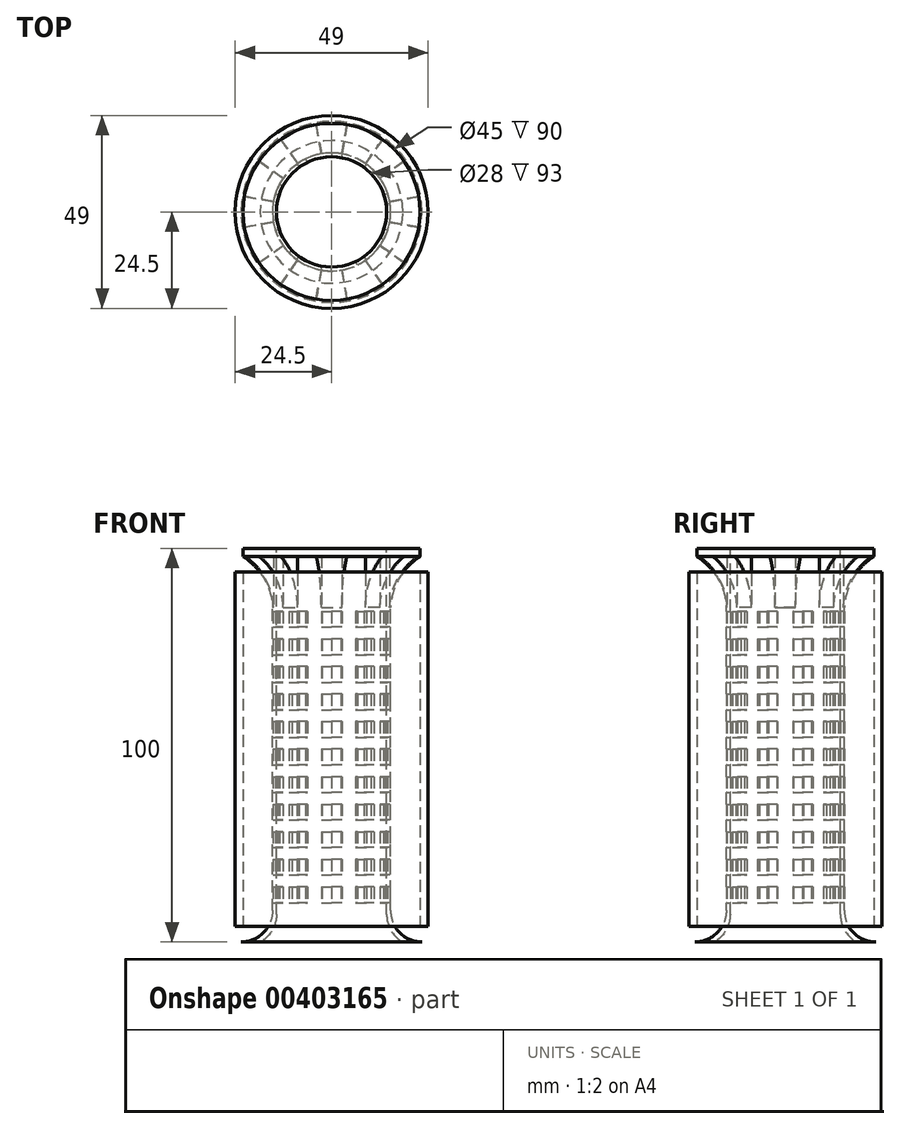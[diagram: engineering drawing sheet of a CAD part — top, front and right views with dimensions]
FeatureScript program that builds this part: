
annotation { "Feature Type Name" : "Feature", "Feature Type Description" : "" }
export const myFeature = defineFeature(function(context is Context, id is Id, definition is map)
    precondition{}
    {
        {
            var Q0;
            Q0=qCreatedBy(makeId("Top.planeOp"),FACE);
            var sketch = newSketch(context, id + "F0", { "sketchPlane" : qUnion([Q0])});
            skCircle(sketch, "E0", {"center": v(0, 0) * mm, "radius": 24.5 * mm});
            skCircle(sketch, "E1", {"center": v(0, 0) * mm, "radius": 22.5 * mm});
            skSolve(sketch);
        }
        {
            var Q0;
            Q0=qCreatedBy(makeId("Top.planeOp"),FACE);
            cPlane(context, id + "F1", {"entities" : qUnion([Q0]), "cplaneType" : CPlaneType.OFFSET, "offset" : 50 * mm, "width" : 150 * mm, "height" : 150 * mm});
        }
        {
            var Q0;
            Q0=qCreatedBy(makeId("Top.planeOp"),FACE);
            cPlane(context, id + "F2", {"entities" : qUnion([Q0]), "cplaneType" : CPlaneType.OFFSET, "offset" : 50 * mm, "oppositeDirection" : true, "width" : 150 * mm, "height" : 150 * mm});
        }
        {
            var Q0;
            Q0=qCreatedBy(makeId("Right.planeOp"),FACE);
            var sketch = newSketch(context, id + "F3", { "sketchPlane" : qUnion([Q0])});
            skLineSegment(sketch, "E2", {"start": v(0, 49) * mm, "end": v(0, -49) * mm});
            skLineSegment(sketch, "E3", {"start": v(-22.5, 49) * mm, "end": v(22.5, 49) * mm});
            skLineSegment(sketch, "E4", {"start": v(37, -49) * mm, "end": v(-37, -49) * mm});
            skLineSegment(sketch, "E5", {"start": v(14, 0) * mm, "end": v(-14, 0) * mm});
            skLineSegment(sketch, "E6.bottom", {"start": v(-14, 49) * mm, "end": v(-15, 49) * mm});
            skLineSegment(sketch, "E6.top", {"start": v(-14, -49) * mm, "end": v(-15, -49) * mm});
            skLineSegment(sketch, "E6.left", {"start": v(-14, 49) * mm, "end": v(-14, -49) * mm});
            skLineSegment(sketch, "E6.right", {"start": v(-15, 49) * mm, "end": v(-15, -49) * mm});
            skLineSegment(sketch, "E7.bottom", {"start": v(-23, -49) * mm, "end": v(-37, -49) * mm});
            skLineSegment(sketch, "E7.top", {"start": v(-22, -50) * mm, "end": v(-37, -50) * mm});
            skLineSegment(sketch, "E7.left", {"start": v(-14, -42) * mm, "end": v(-14, -45) * mm});
            skLineSegment(sketch, "E7.right", {"start": v(-37, -49) * mm, "end": v(-37, -50) * mm});
            skLineSegment(sketch, "E8.bottom", {"start": v(-37, -49) * mm, "end": v(-36, -49) * mm});
            skLineSegment(sketch, "E8.top", {"start": v(-37, -44) * mm, "end": v(-36, -44) * mm});
            skLineSegment(sketch, "E8.left", {"start": v(-37, -49) * mm, "end": v(-37, -44) * mm});
            skLineSegment(sketch, "E8.right", {"start": v(-36, -49) * mm, "end": v(-36, -44) * mm});
            skPoint(sketch, "E9.visualSharp", {"position": v(-14, -50) * mm});
            skArc(sketch, "E9.filletArc", {"start": v(-22, -50) * mm, "mid": v(-16.34, -47.66) * mm, "end": v(-14, -42) * mm});
            skLineSegment(sketch, "E10.bottom", {"start": v(-22.5, 49) * mm, "end": v(-14, 49) * mm});
            skLineSegment(sketch, "E10.top", {"start": v(-22.5, 51) * mm, "end": v(-14, 51) * mm});
            skLineSegment(sketch, "E10.left", {"start": v(-22.5, 49) * mm, "end": v(-22.5, 51) * mm});
            skLineSegment(sketch, "E10.right", {"start": v(-14, 49) * mm, "end": v(-14, 51) * mm});
            skLineSegment(sketch, "E11", {"start": v(-15, 36) * mm, "end": v(-22.5, 49) * mm});
            skLineSegment(sketch, "E12.bottom", {"start": v(-22.5, 51) * mm, "end": v(-21.5, 51) * mm});
            skLineSegment(sketch, "E12.top", {"start": v(-22.5, 59) * mm, "end": v(-21.5, 59) * mm});
            skLineSegment(sketch, "E12.left", {"start": v(-22.5, 51) * mm, "end": v(-22.5, 59) * mm});
            skLineSegment(sketch, "E12.right", {"start": v(-21.5, 51) * mm, "end": v(-21.5, 59) * mm});
            skLineSegment(sketch, "E13.bottom", {"start": v(-15, -46) * mm, "end": v(-14, -46) * mm});
            skLineSegment(sketch, "E13.top", {"start": v(-15, -49) * mm, "end": v(-14, -49) * mm});
            skLineSegment(sketch, "E13.left", {"start": v(-15, -46) * mm, "end": v(-15, -49) * mm});
            skLineSegment(sketch, "E13.right", {"start": v(-14, -46) * mm, "end": v(-14, -49) * mm});
            skLineSegment(sketch, "E14.0.1.0", {"start": v(-15, -42) * mm, "end": v(-14, -42) * mm});
            skLineSegment(sketch, "E14.0.1.1", {"start": v(-15, -39) * mm, "end": v(-14, -39) * mm});
            skLineSegment(sketch, "E14.0.2.0", {"start": v(-15, -35) * mm, "end": v(-14, -35) * mm});
            skLineSegment(sketch, "E14.0.2.1", {"start": v(-15, -32) * mm, "end": v(-14, -32) * mm});
            skLineSegment(sketch, "E14.0.3.0", {"start": v(-15, -28) * mm, "end": v(-14, -28) * mm});
            skLineSegment(sketch, "E14.0.3.1", {"start": v(-15, -25) * mm, "end": v(-14, -25) * mm});
            skLineSegment(sketch, "E14.0.4.0", {"start": v(-15, -21) * mm, "end": v(-14, -21) * mm});
            skLineSegment(sketch, "E14.0.4.1", {"start": v(-15, -18) * mm, "end": v(-14, -18) * mm});
            skLineSegment(sketch, "E14.0.5.0", {"start": v(-15, -14) * mm, "end": v(-14, -14) * mm});
            skLineSegment(sketch, "E14.0.5.1", {"start": v(-15, -11) * mm, "end": v(-14, -11) * mm});
            skLineSegment(sketch, "E14.0.6.0", {"start": v(-15, -7) * mm, "end": v(-14, -7) * mm});
            skLineSegment(sketch, "E14.0.6.1", {"start": v(-15, -4) * mm, "end": v(-14, -4) * mm});
            skLineSegment(sketch, "E14.0.7.0", {"start": v(-15, 0) * mm, "end": v(-14, 0) * mm});
            skLineSegment(sketch, "E14.0.7.1", {"start": v(-15, 3) * mm, "end": v(-14, 3) * mm});
            skLineSegment(sketch, "E14.0.8.0", {"start": v(-15, 7) * mm, "end": v(-14, 7) * mm});
            skLineSegment(sketch, "E14.0.8.1", {"start": v(-15, 10) * mm, "end": v(-14, 10) * mm});
            skLineSegment(sketch, "E14.0.9.0", {"start": v(-15, 14) * mm, "end": v(-14, 14) * mm});
            skLineSegment(sketch, "E14.0.9.1", {"start": v(-15, 17) * mm, "end": v(-14, 17) * mm});
            skLineSegment(sketch, "E14.0.10.0", {"start": v(-15, 21) * mm, "end": v(-14, 21) * mm});
            skLineSegment(sketch, "E14.0.10.1", {"start": v(-15, 24) * mm, "end": v(-14, 24) * mm});
            skLineSegment(sketch, "E14.0.11.0", {"start": v(-15, 28) * mm, "end": v(-14, 28) * mm});
            skLineSegment(sketch, "E14.0.11.1", {"start": v(-15, 31) * mm, "end": v(-14, 31) * mm});
            skLineSegment(sketch, "E14.0.12.0", {"start": v(-15, 35) * mm, "end": v(-14, 35) * mm});
            skLineSegment(sketch, "E14.0.12.1", {"start": v(-15, 38) * mm, "end": v(-14, 38) * mm});
            skLineSegment(sketch, "E14.direction1", {"start": v(-16, -49) * mm, "end": v(9, -49) * mm, "construction": true});
            skLineSegment(sketch, "E14.direction2", {"start": v(-15, -42) * mm, "end": v(-15, -41) * mm, "construction": true});
            skPoint(sketch, "E15.newPointB", {"position": v(-15, -49) * mm});
            skArc(sketch, "E15.filletArc", {"start": v(-23, -49) * mm, "mid": v(-17.34, -46.66) * mm, "end": v(-15, -41) * mm});
            skArc(sketch, "E16", {"start": v(-15, 36) * mm, "mid": v(-17.17, 43.42) * mm, "end": v(-22.5, 49) * mm});
            skSolve(sketch);
        }
        {
            var Q0;
            Q0=makeQuery(id+"F3.imprint","IMPRINT",FACE,{"disambiguationData":[TD([[makeQuery(id+"F3.imprint","IMPRINT",EDGE,{"derivedFrom":sQuery(id+"F3.wireOp",EDGE,"E12.bottom")}),1.0]])]});
            var Q1;
            {var subQ0=sQuery(id+"F3.wireOp",EDGE,"E14.0.8.1");Q1=makeQuery(id+"F3.imprint","IMPRINT",FACE,{"disambiguationData":[TD([[makeQuery(id+"F3.imprint","IMPRINT",EDGE,{"derivedFrom":subQ0}),1.0]])]});}
            var Q2;
            {var subQ0=sQuery(id+"F3.wireOp",EDGE,"E14.0.7.1");Q2=makeQuery(id+"F3.imprint","IMPRINT",FACE,{"disambiguationData":[TD([[makeQuery(id+"F3.imprint","IMPRINT",EDGE,{"derivedFrom":subQ0}),1.0]])]});}
            var Q3;
            {var subQ0=sQuery(id+"F3.wireOp",EDGE,"E14.0.11.1");Q3=makeQuery(id+"F3.imprint","IMPRINT",FACE,{"disambiguationData":[TD([[makeQuery(id+"F3.imprint","IMPRINT",EDGE,{"derivedFrom":subQ0}),1.0]])]});}
            var Q4;
            {var subQ3=sQuery(id+"F3.wireOp",EDGE,"E14.0.12.1");Q4=makeQuery(id+"F3.imprint","IMPRINT",FACE,{"disambiguationData":[TD([[makeQuery(id+"F3.imprint","IMPRINT",EDGE,{"derivedFrom":subQ3}),1.0]])]});}
            var Q5;
            {var subQ0=sQuery(id+"F3.wireOp",EDGE,"E14.0.4.1");Q5=makeQuery(id+"F3.imprint","IMPRINT",FACE,{"disambiguationData":[TD([[makeQuery(id+"F3.imprint","IMPRINT",EDGE,{"derivedFrom":subQ0}),1.0]])]});}
            var Q6;
            {var subQ0=sQuery(id+"F3.wireOp",EDGE,"E14.0.9.1");Q6=makeQuery(id+"F3.imprint","IMPRINT",FACE,{"disambiguationData":[TD([[makeQuery(id+"F3.imprint","IMPRINT",EDGE,{"derivedFrom":subQ0}),1.0]])]});}
            var Q7;
            {var subQ0=sQuery(id+"F3.wireOp",EDGE,"E14.0.3.1");Q7=makeQuery(id+"F3.imprint","IMPRINT",FACE,{"disambiguationData":[TD([[makeQuery(id+"F3.imprint","IMPRINT",EDGE,{"derivedFrom":subQ0}),1.0]])]});}
            var Q8;
            {var subQ0=sQuery(id+"F3.wireOp",EDGE,"E14.0.10.1");Q8=makeQuery(id+"F3.imprint","IMPRINT",FACE,{"disambiguationData":[TD([[makeQuery(id+"F3.imprint","IMPRINT",EDGE,{"derivedFrom":subQ0}),1.0]])]});}
            var Q9;
            Q9=makeQuery(id+"F3.imprint","IMPRINT",FACE,{"disambiguationData":[TD([[makeQuery(id+"F3.imprint","IMPRINT",EDGE,{"derivedFrom":sQuery(id+"F3.wireOp",EDGE,"E10.top")}),-1.0]])]});
            var Q10;
            {var subQ0=sQuery(id+"F3.wireOp",EDGE,"E14.0.2.1");Q10=makeQuery(id+"F3.imprint","IMPRINT",FACE,{"disambiguationData":[TD([[makeQuery(id+"F3.imprint","IMPRINT",EDGE,{"derivedFrom":subQ0}),1.0]])]});}
            var Q11;
            {var subQ0=sQuery(id+"F3.wireOp",EDGE,"E14.0.1.1");Q11=makeQuery(id+"F3.imprint","IMPRINT",FACE,{"disambiguationData":[TD([[makeQuery(id+"F3.imprint","IMPRINT",EDGE,{"derivedFrom":subQ0}),1.0]])]});}
            var Q12;
            {var subQ0=sQuery(id+"F3.wireOp",EDGE,"E14.0.6.0");Q12=makeQuery(id+"F3.imprint","IMPRINT",FACE,{"disambiguationData":[TD([[makeQuery(id+"F3.imprint","IMPRINT",EDGE,{"derivedFrom":subQ0}),1.0]])]});}
            var Q13;
            {var subQ0=sQuery(id+"F3.wireOp",EDGE,"E14.0.8.0");Q13=makeQuery(id+"F3.imprint","IMPRINT",FACE,{"disambiguationData":[TD([[makeQuery(id+"F3.imprint","IMPRINT",EDGE,{"derivedFrom":subQ0}),1.0]])]});}
            var Q14;
            {var subQ0=sQuery(id+"F3.wireOp",EDGE,"E14.0.3.0");Q14=makeQuery(id+"F3.imprint","IMPRINT",FACE,{"disambiguationData":[TD([[makeQuery(id+"F3.imprint","IMPRINT",EDGE,{"derivedFrom":subQ0}),1.0]])]});}
            var Q15;
            {var subQ2=sQuery(id+"F3.wireOp",EDGE,"E14.0.6.1");Q15=makeQuery(id+"F3.imprint","IMPRINT",FACE,{"disambiguationData":[TD([[makeQuery(id+"F3.imprint","IMPRINT",EDGE,{"derivedFrom":subQ2}),1.0]])]});}
            var Q16;
            {var subQ0=sQuery(id+"F3.wireOp",EDGE,"E14.0.9.0");Q16=makeQuery(id+"F3.imprint","IMPRINT",FACE,{"disambiguationData":[TD([[makeQuery(id+"F3.imprint","IMPRINT",EDGE,{"derivedFrom":subQ0}),1.0]])]});}
            var Q17;
            {var subQ0=sQuery(id+"F3.wireOp",EDGE,"E14.0.5.1");Q17=makeQuery(id+"F3.imprint","IMPRINT",FACE,{"disambiguationData":[TD([[makeQuery(id+"F3.imprint","IMPRINT",EDGE,{"derivedFrom":subQ0}),1.0]])]});}
            var Q18;
            {var subQ0=sQuery(id+"F3.wireOp",EDGE,"E14.0.1.0");Q18=makeQuery(id+"F3.imprint","IMPRINT",FACE,{"disambiguationData":[TD([[makeQuery(id+"F3.imprint","IMPRINT",EDGE,{"derivedFrom":subQ0}),1.0]])]});}
            var Q19;
            {var subQ0=sQuery(id+"F3.wireOp",EDGE,"E14.0.10.0");Q19=makeQuery(id+"F3.imprint","IMPRINT",FACE,{"disambiguationData":[TD([[makeQuery(id+"F3.imprint","IMPRINT",EDGE,{"derivedFrom":subQ0}),1.0]])]});}
            var Q20;
            {var subQ0=sQuery(id+"F3.wireOp",EDGE,"E14.0.11.0");Q20=makeQuery(id+"F3.imprint","IMPRINT",FACE,{"disambiguationData":[TD([[makeQuery(id+"F3.imprint","IMPRINT",EDGE,{"derivedFrom":subQ0}),1.0]])]});}
            var Q21;
            {var subQ0=sQuery(id+"F3.wireOp",EDGE,"E14.0.7.0");Q21=makeQuery(id+"F3.imprint","IMPRINT",FACE,{"disambiguationData":[TD([[makeQuery(id+"F3.imprint","IMPRINT",EDGE,{"derivedFrom":subQ0}),1.0]])]});}
            var Q22;
            {var subQ0=sQuery(id+"F3.wireOp",EDGE,"E14.0.4.0");Q22=makeQuery(id+"F3.imprint","IMPRINT",FACE,{"disambiguationData":[TD([[makeQuery(id+"F3.imprint","IMPRINT",EDGE,{"derivedFrom":subQ0}),1.0]])]});}
            var Q23;
            {var subQ2=sQuery(id+"F3.wireOp",EDGE,"E14.0.12.0");Q23=makeQuery(id+"F3.imprint","IMPRINT",FACE,{"disambiguationData":[TD([[makeQuery(id+"F3.imprint","IMPRINT",EDGE,{"derivedFrom":subQ2}),1.0]])]});}
            var Q24;
            {var subQ0=sQuery(id+"F3.wireOp",EDGE,"E14.0.2.0");Q24=makeQuery(id+"F3.imprint","IMPRINT",FACE,{"disambiguationData":[TD([[makeQuery(id+"F3.imprint","IMPRINT",EDGE,{"derivedFrom":subQ0}),1.0]])]});}
            var Q25;
            {var subQ0=sQuery(id+"F3.wireOp",EDGE,"E14.0.5.0");Q25=makeQuery(id+"F3.imprint","IMPRINT",FACE,{"disambiguationData":[TD([[makeQuery(id+"F3.imprint","IMPRINT",EDGE,{"derivedFrom":subQ0}),1.0]])]});}
            var Q26;
            Q26=makeQuery(id+"F3.imprint","IMPRINT",FACE,{"disambiguationData":[TD([[makeQuery(id+"F3.imprint","IMPRINT",EDGE,{"derivedFrom":sQuery(id+"F3.wireOp",EDGE,"E7.bottom")}),1.0]])]});
            var Q27;
            Q27=makeQuery(id+"F3.imprint","IMPRINT",FACE,{"disambiguationData":[TD([[makeQuery(id+"F3.imprint","IMPRINT",EDGE,{"derivedFrom":sQuery(id+"F3.wireOp",EDGE,"E8.bottom")}),1.0]])]});
            var Q28;
            {var subQ6=sQuery(id+"F3.wireOp",EDGE,"E15.filletArc");Q28=makeQuery(id+"F3.imprint","IMPRINT",FACE,{"disambiguationData":[TD([[makeQuery(id+"F3.imprint","IMPRINT",EDGE,{"derivedFrom":subQ6}),-1.0]])]});}
            var Q29;
            {var subQ0=sQuery(id+"F3.wireOp",EDGE,"E14.0.1.0");Q29=makeQuery(id+"F3.imprint","IMPRINT",FACE,{"disambiguationData":[TD([[makeQuery(id+"F3.imprint","IMPRINT",EDGE,{"derivedFrom":subQ0}),-1.0]])]});}
            var Q30;
            Q30=sQuery(id+"F3.wireOp",EDGE,"E2");
            revolve(context, id + "F4", {"entities" : qUnion([Q0, Q1, Q2, Q3, Q4, Q5, Q6, Q7, Q8, Q9, Q10, Q11, Q12, Q13, Q14, Q15, Q16, Q17, Q18, Q19, Q20, Q21, Q22, Q23, Q24, Q25, Q26, Q27, Q28, Q29]), "axis" : qUnion([Q30]), "revolveType" : RevolveType.FULL});
        }
        {
            var Q0;
            {var subQ0=sQuery(id+"F3.wireOp",EDGE,"E13.bottom");Q0=makeQuery(id+"F3.imprint","IMPRINT",FACE,{"disambiguationData":[TD([[makeQuery(id+"F3.imprint","IMPRINT",EDGE,{"derivedFrom":subQ0}),1.0]])]});}
            var Q1;
            {var subQ0=sQuery(id+"F3.wireOp",EDGE,"E14.0.1.1");Q1=makeQuery(id+"F3.imprint","IMPRINT",FACE,{"disambiguationData":[TD([[makeQuery(id+"F3.imprint","IMPRINT",EDGE,{"derivedFrom":subQ0}),1.0]])]});}
            var Q2;
            {var subQ0=sQuery(id+"F3.wireOp",EDGE,"E14.0.2.1");Q2=makeQuery(id+"F3.imprint","IMPRINT",FACE,{"disambiguationData":[TD([[makeQuery(id+"F3.imprint","IMPRINT",EDGE,{"derivedFrom":subQ0}),1.0]])]});}
            var Q3;
            {var subQ0=sQuery(id+"F3.wireOp",EDGE,"E14.0.3.1");Q3=makeQuery(id+"F3.imprint","IMPRINT",FACE,{"disambiguationData":[TD([[makeQuery(id+"F3.imprint","IMPRINT",EDGE,{"derivedFrom":subQ0}),1.0]])]});}
            var Q4;
            {var subQ0=sQuery(id+"F3.wireOp",EDGE,"E14.0.4.1");Q4=makeQuery(id+"F3.imprint","IMPRINT",FACE,{"disambiguationData":[TD([[makeQuery(id+"F3.imprint","IMPRINT",EDGE,{"derivedFrom":subQ0}),1.0]])]});}
            var Q5;
            {var subQ0=sQuery(id+"F3.wireOp",EDGE,"E14.0.5.1");Q5=makeQuery(id+"F3.imprint","IMPRINT",FACE,{"disambiguationData":[TD([[makeQuery(id+"F3.imprint","IMPRINT",EDGE,{"derivedFrom":subQ0}),1.0]])]});}
            var Q6;
            {var subQ2=sQuery(id+"F3.wireOp",EDGE,"E14.0.6.1");Q6=makeQuery(id+"F3.imprint","IMPRINT",FACE,{"disambiguationData":[TD([[makeQuery(id+"F3.imprint","IMPRINT",EDGE,{"derivedFrom":subQ2}),1.0]])]});}
            var Q7;
            {var subQ0=sQuery(id+"F3.wireOp",EDGE,"E14.0.7.1");Q7=makeQuery(id+"F3.imprint","IMPRINT",FACE,{"disambiguationData":[TD([[makeQuery(id+"F3.imprint","IMPRINT",EDGE,{"derivedFrom":subQ0}),1.0]])]});}
            var Q8;
            {var subQ0=sQuery(id+"F3.wireOp",EDGE,"E14.0.8.1");Q8=makeQuery(id+"F3.imprint","IMPRINT",FACE,{"disambiguationData":[TD([[makeQuery(id+"F3.imprint","IMPRINT",EDGE,{"derivedFrom":subQ0}),1.0]])]});}
            var Q9;
            {var subQ0=sQuery(id+"F3.wireOp",EDGE,"E14.0.9.1");Q9=makeQuery(id+"F3.imprint","IMPRINT",FACE,{"disambiguationData":[TD([[makeQuery(id+"F3.imprint","IMPRINT",EDGE,{"derivedFrom":subQ0}),1.0]])]});}
            var Q10;
            {var subQ0=sQuery(id+"F3.wireOp",EDGE,"E14.0.10.1");Q10=makeQuery(id+"F3.imprint","IMPRINT",FACE,{"disambiguationData":[TD([[makeQuery(id+"F3.imprint","IMPRINT",EDGE,{"derivedFrom":subQ0}),1.0]])]});}
            var Q11;
            {var subQ0=sQuery(id+"F3.wireOp",EDGE,"E14.0.11.1");Q11=makeQuery(id+"F3.imprint","IMPRINT",FACE,{"disambiguationData":[TD([[makeQuery(id+"F3.imprint","IMPRINT",EDGE,{"derivedFrom":subQ0}),1.0]])]});}
            var Q12;
            Q12=sQuery(id+"F3.wireOp",EDGE,"E2");
            revolve(context, id + "F5", {"entities" : qUnion([Q0, Q1, Q2, Q3, Q4, Q5, Q6, Q7, Q8, Q9, Q10, Q11]), "axis" : qUnion([Q12]), "revolveType" : RevolveType.ONE_DIRECTION, "angle" : 10 * degree});
        }
        {
            var Q0;
            Q0=makeQuery(id+"F5.opRevolve","SWEPT_BODY",BODY,{"disambiguationData":[OSD([sQuery(id+"F3.wireOp",EDGE,"E6.left"),sQuery(id+"F3.wireOp",EDGE,"E6.right"),sQuery(id+"F3.wireOp",EDGE,"E14.0.11.1"),sQuery(id+"F3.wireOp",EDGE,"E14.0.12.0")])]});
            var Q1;
            Q1=makeQuery(id+"F5.opRevolve","SWEPT_BODY",BODY,{"disambiguationData":[OSD([sQuery(id+"F3.wireOp",EDGE,"E6.left"),sQuery(id+"F3.wireOp",EDGE,"E6.right"),sQuery(id+"F3.wireOp",EDGE,"E14.0.10.1"),sQuery(id+"F3.wireOp",EDGE,"E14.0.11.0")])]});
            var Q2;
            Q2=makeQuery(id+"F5.opRevolve","SWEPT_BODY",BODY,{"disambiguationData":[OSD([sQuery(id+"F3.wireOp",EDGE,"E6.left"),sQuery(id+"F3.wireOp",EDGE,"E6.right"),sQuery(id+"F3.wireOp",EDGE,"E14.0.9.1"),sQuery(id+"F3.wireOp",EDGE,"E14.0.10.0")])]});
            var Q3;
            Q3=makeQuery(id+"F5.opRevolve","SWEPT_BODY",BODY,{"disambiguationData":[OSD([sQuery(id+"F3.wireOp",EDGE,"E6.left"),sQuery(id+"F3.wireOp",EDGE,"E6.right"),sQuery(id+"F3.wireOp",EDGE,"E14.0.8.1"),sQuery(id+"F3.wireOp",EDGE,"E14.0.9.0")])]});
            var Q4;
            Q4=makeQuery(id+"F5.opRevolve","SWEPT_BODY",BODY,{"disambiguationData":[OSD([sQuery(id+"F3.wireOp",EDGE,"E6.left"),sQuery(id+"F3.wireOp",EDGE,"E6.right"),sQuery(id+"F3.wireOp",EDGE,"E14.0.7.1"),sQuery(id+"F3.wireOp",EDGE,"E14.0.8.0")])]});
            var Q5;
            Q5=makeQuery(id+"F5.opRevolve","SWEPT_BODY",BODY,{"disambiguationData":[OSD([sQuery(id+"F3.wireOp",EDGE,"E6.left"),sQuery(id+"F3.wireOp",EDGE,"E6.right"),sQuery(id+"F3.wireOp",EDGE,"E14.0.6.1"),sQuery(id+"F3.wireOp",EDGE,"E14.0.7.0")])]});
            var Q6;
            Q6=makeQuery(id+"F5.opRevolve","SWEPT_BODY",BODY,{"disambiguationData":[OSD([sQuery(id+"F3.wireOp",EDGE,"E6.left"),sQuery(id+"F3.wireOp",EDGE,"E6.right"),sQuery(id+"F3.wireOp",EDGE,"E14.0.5.1"),sQuery(id+"F3.wireOp",EDGE,"E14.0.6.0")])]});
            var Q7;
            Q7=makeQuery(id+"F5.opRevolve","SWEPT_BODY",BODY,{"disambiguationData":[OSD([sQuery(id+"F3.wireOp",EDGE,"E6.left"),sQuery(id+"F3.wireOp",EDGE,"E6.right"),sQuery(id+"F3.wireOp",EDGE,"E14.0.4.1"),sQuery(id+"F3.wireOp",EDGE,"E14.0.5.0")])]});
            var Q8;
            Q8=makeQuery(id+"F5.opRevolve","SWEPT_BODY",BODY,{"disambiguationData":[OSD([sQuery(id+"F3.wireOp",EDGE,"E6.left"),sQuery(id+"F3.wireOp",EDGE,"E6.right"),sQuery(id+"F3.wireOp",EDGE,"E14.0.3.1"),sQuery(id+"F3.wireOp",EDGE,"E14.0.4.0")])]});
            var Q9;
            Q9=makeQuery(id+"F5.opRevolve","SWEPT_BODY",BODY,{"disambiguationData":[OSD([sQuery(id+"F3.wireOp",EDGE,"E6.left"),sQuery(id+"F3.wireOp",EDGE,"E6.right"),sQuery(id+"F3.wireOp",EDGE,"E14.0.2.1"),sQuery(id+"F3.wireOp",EDGE,"E14.0.3.0")])]});
            var Q10;
            Q10=makeQuery(id+"F5.opRevolve","SWEPT_BODY",BODY,{"disambiguationData":[OSD([sQuery(id+"F3.wireOp",EDGE,"E6.left"),sQuery(id+"F3.wireOp",EDGE,"E6.right"),sQuery(id+"F3.wireOp",EDGE,"E14.0.1.1"),sQuery(id+"F3.wireOp",EDGE,"E14.0.2.0")])]});
            var Q11;
            Q11=makeQuery(id+"F5.opRevolve","SWEPT_BODY",BODY,{"disambiguationData":[OSD([sQuery(id+"F3.wireOp",EDGE,"E6.left"),sQuery(id+"F3.wireOp",EDGE,"E6.right"),sQuery(id+"F3.wireOp",EDGE,"E13.bottom"),sQuery(id+"F3.wireOp",EDGE,"E14.0.1.0")])]});
            var Q12;
            Q12=sQuery(id+"F3.wireOp",EDGE,"E2");
            circularPattern(context, id + "F6", {"entities" : qUnion([Q0, Q1, Q2, Q3, Q4, Q5, Q6, Q7, Q8, Q9, Q10, Q11]), "axis" : qUnion([Q12]), "angle" : 360 * degree, "instanceCount" : 10, "equalSpace" : true});
        }
        {
            var Q0;
            Q0=makeQuery(id+"F6.opPattern","COPY",BODY,{"derivedFrom":makeQuery(id+"F5.opRevolve","SWEPT_BODY",BODY,{"disambiguationData":[OSD([sQuery(id+"F3.wireOp",EDGE,"E6.left"),sQuery(id+"F3.wireOp",EDGE,"E6.right"),sQuery(id+"F3.wireOp",EDGE,"E14.0.2.1"),sQuery(id+"F3.wireOp",EDGE,"E14.0.3.0")])]}),"instanceName":"9"});
            var Q1;
            Q1=makeQuery(id+"F5.opRevolve","SWEPT_BODY",BODY,{"disambiguationData":[OSD([sQuery(id+"F3.wireOp",EDGE,"E6.left"),sQuery(id+"F3.wireOp",EDGE,"E6.right"),sQuery(id+"F3.wireOp",EDGE,"E14.0.10.1"),sQuery(id+"F3.wireOp",EDGE,"E14.0.11.0")])]});
            var Q2;
            Q2=makeQuery(id+"F5.opRevolve","SWEPT_BODY",BODY,{"disambiguationData":[OSD([sQuery(id+"F3.wireOp",EDGE,"E6.left"),sQuery(id+"F3.wireOp",EDGE,"E6.right"),sQuery(id+"F3.wireOp",EDGE,"E14.0.9.1"),sQuery(id+"F3.wireOp",EDGE,"E14.0.10.0")])]});
            var Q3;
            Q3=makeQuery(id+"F5.opRevolve","SWEPT_BODY",BODY,{"disambiguationData":[OSD([sQuery(id+"F3.wireOp",EDGE,"E6.left"),sQuery(id+"F3.wireOp",EDGE,"E6.right"),sQuery(id+"F3.wireOp",EDGE,"E14.0.8.1"),sQuery(id+"F3.wireOp",EDGE,"E14.0.9.0")])]});
            var Q4;
            Q4=makeQuery(id+"F5.opRevolve","SWEPT_BODY",BODY,{"disambiguationData":[OSD([sQuery(id+"F3.wireOp",EDGE,"E6.left"),sQuery(id+"F3.wireOp",EDGE,"E6.right"),sQuery(id+"F3.wireOp",EDGE,"E14.0.7.1"),sQuery(id+"F3.wireOp",EDGE,"E14.0.8.0")])]});
            var Q5;
            Q5=makeQuery(id+"F5.opRevolve","SWEPT_BODY",BODY,{"disambiguationData":[OSD([sQuery(id+"F3.wireOp",EDGE,"E6.left"),sQuery(id+"F3.wireOp",EDGE,"E6.right"),sQuery(id+"F3.wireOp",EDGE,"E14.0.6.1"),sQuery(id+"F3.wireOp",EDGE,"E14.0.7.0")])]});
            var Q6;
            Q6=makeQuery(id+"F5.opRevolve","SWEPT_BODY",BODY,{"disambiguationData":[OSD([sQuery(id+"F3.wireOp",EDGE,"E6.left"),sQuery(id+"F3.wireOp",EDGE,"E6.right"),sQuery(id+"F3.wireOp",EDGE,"E14.0.5.1"),sQuery(id+"F3.wireOp",EDGE,"E14.0.6.0")])]});
            var Q7;
            Q7=makeQuery(id+"F5.opRevolve","SWEPT_BODY",BODY,{"disambiguationData":[OSD([sQuery(id+"F3.wireOp",EDGE,"E6.left"),sQuery(id+"F3.wireOp",EDGE,"E6.right"),sQuery(id+"F3.wireOp",EDGE,"E14.0.4.1"),sQuery(id+"F3.wireOp",EDGE,"E14.0.5.0")])]});
            var Q8;
            Q8=makeQuery(id+"F5.opRevolve","SWEPT_BODY",BODY,{"disambiguationData":[OSD([sQuery(id+"F3.wireOp",EDGE,"E6.left"),sQuery(id+"F3.wireOp",EDGE,"E6.right"),sQuery(id+"F3.wireOp",EDGE,"E14.0.3.1"),sQuery(id+"F3.wireOp",EDGE,"E14.0.4.0")])]});
            var Q9;
            Q9=makeQuery(id+"F5.opRevolve","SWEPT_BODY",BODY,{"disambiguationData":[OSD([sQuery(id+"F3.wireOp",EDGE,"E6.left"),sQuery(id+"F3.wireOp",EDGE,"E6.right"),sQuery(id+"F3.wireOp",EDGE,"E14.0.2.1"),sQuery(id+"F3.wireOp",EDGE,"E14.0.3.0")])]});
            var Q10;
            Q10=makeQuery(id+"F5.opRevolve","SWEPT_BODY",BODY,{"disambiguationData":[OSD([sQuery(id+"F3.wireOp",EDGE,"E6.left"),sQuery(id+"F3.wireOp",EDGE,"E6.right"),sQuery(id+"F3.wireOp",EDGE,"E14.0.1.1"),sQuery(id+"F3.wireOp",EDGE,"E14.0.2.0")])]});
            var Q11;
            Q11=makeQuery(id+"F5.opRevolve","SWEPT_BODY",BODY,{"disambiguationData":[OSD([sQuery(id+"F3.wireOp",EDGE,"E6.left"),sQuery(id+"F3.wireOp",EDGE,"E6.right"),sQuery(id+"F3.wireOp",EDGE,"E13.bottom"),sQuery(id+"F3.wireOp",EDGE,"E14.0.1.0")])]});
            var Q12;
            Q12=makeQuery(id+"F6.opPattern","COPY",BODY,{"derivedFrom":makeQuery(id+"F5.opRevolve","SWEPT_BODY",BODY,{"disambiguationData":[OSD([sQuery(id+"F3.wireOp",EDGE,"E6.left"),sQuery(id+"F3.wireOp",EDGE,"E6.right"),sQuery(id+"F3.wireOp",EDGE,"E14.0.11.1"),sQuery(id+"F3.wireOp",EDGE,"E14.0.12.0")])]}),"instanceName":"1"});
            var Q13;
            Q13=makeQuery(id+"F6.opPattern","COPY",BODY,{"derivedFrom":makeQuery(id+"F5.opRevolve","SWEPT_BODY",BODY,{"disambiguationData":[OSD([sQuery(id+"F3.wireOp",EDGE,"E6.left"),sQuery(id+"F3.wireOp",EDGE,"E6.right"),sQuery(id+"F3.wireOp",EDGE,"E14.0.10.1"),sQuery(id+"F3.wireOp",EDGE,"E14.0.11.0")])]}),"instanceName":"1"});
            var Q14;
            Q14=makeQuery(id+"F6.opPattern","COPY",BODY,{"derivedFrom":makeQuery(id+"F5.opRevolve","SWEPT_BODY",BODY,{"disambiguationData":[OSD([sQuery(id+"F3.wireOp",EDGE,"E6.left"),sQuery(id+"F3.wireOp",EDGE,"E6.right"),sQuery(id+"F3.wireOp",EDGE,"E14.0.9.1"),sQuery(id+"F3.wireOp",EDGE,"E14.0.10.0")])]}),"instanceName":"1"});
            var Q15;
            Q15=makeQuery(id+"F6.opPattern","COPY",BODY,{"derivedFrom":makeQuery(id+"F5.opRevolve","SWEPT_BODY",BODY,{"disambiguationData":[OSD([sQuery(id+"F3.wireOp",EDGE,"E6.left"),sQuery(id+"F3.wireOp",EDGE,"E6.right"),sQuery(id+"F3.wireOp",EDGE,"E14.0.8.1"),sQuery(id+"F3.wireOp",EDGE,"E14.0.9.0")])]}),"instanceName":"1"});
            var Q16;
            Q16=makeQuery(id+"F6.opPattern","COPY",BODY,{"derivedFrom":makeQuery(id+"F5.opRevolve","SWEPT_BODY",BODY,{"disambiguationData":[OSD([sQuery(id+"F3.wireOp",EDGE,"E6.left"),sQuery(id+"F3.wireOp",EDGE,"E6.right"),sQuery(id+"F3.wireOp",EDGE,"E14.0.7.1"),sQuery(id+"F3.wireOp",EDGE,"E14.0.8.0")])]}),"instanceName":"1"});
            var Q17;
            Q17=makeQuery(id+"F6.opPattern","COPY",BODY,{"derivedFrom":makeQuery(id+"F5.opRevolve","SWEPT_BODY",BODY,{"disambiguationData":[OSD([sQuery(id+"F3.wireOp",EDGE,"E6.left"),sQuery(id+"F3.wireOp",EDGE,"E6.right"),sQuery(id+"F3.wireOp",EDGE,"E14.0.6.1"),sQuery(id+"F3.wireOp",EDGE,"E14.0.7.0")])]}),"instanceName":"1"});
            var Q18;
            Q18=makeQuery(id+"F6.opPattern","COPY",BODY,{"derivedFrom":makeQuery(id+"F5.opRevolve","SWEPT_BODY",BODY,{"disambiguationData":[OSD([sQuery(id+"F3.wireOp",EDGE,"E6.left"),sQuery(id+"F3.wireOp",EDGE,"E6.right"),sQuery(id+"F3.wireOp",EDGE,"E14.0.5.1"),sQuery(id+"F3.wireOp",EDGE,"E14.0.6.0")])]}),"instanceName":"1"});
            var Q19;
            Q19=makeQuery(id+"F6.opPattern","COPY",BODY,{"derivedFrom":makeQuery(id+"F5.opRevolve","SWEPT_BODY",BODY,{"disambiguationData":[OSD([sQuery(id+"F3.wireOp",EDGE,"E6.left"),sQuery(id+"F3.wireOp",EDGE,"E6.right"),sQuery(id+"F3.wireOp",EDGE,"E14.0.4.1"),sQuery(id+"F3.wireOp",EDGE,"E14.0.5.0")])]}),"instanceName":"1"});
            var Q20;
            Q20=makeQuery(id+"F6.opPattern","COPY",BODY,{"derivedFrom":makeQuery(id+"F5.opRevolve","SWEPT_BODY",BODY,{"disambiguationData":[OSD([sQuery(id+"F3.wireOp",EDGE,"E6.left"),sQuery(id+"F3.wireOp",EDGE,"E6.right"),sQuery(id+"F3.wireOp",EDGE,"E14.0.3.1"),sQuery(id+"F3.wireOp",EDGE,"E14.0.4.0")])]}),"instanceName":"1"});
            var Q21;
            Q21=makeQuery(id+"F6.opPattern","COPY",BODY,{"derivedFrom":makeQuery(id+"F5.opRevolve","SWEPT_BODY",BODY,{"disambiguationData":[OSD([sQuery(id+"F3.wireOp",EDGE,"E6.left"),sQuery(id+"F3.wireOp",EDGE,"E6.right"),sQuery(id+"F3.wireOp",EDGE,"E14.0.2.1"),sQuery(id+"F3.wireOp",EDGE,"E14.0.3.0")])]}),"instanceName":"1"});
            var Q22;
            Q22=makeQuery(id+"F6.opPattern","COPY",BODY,{"derivedFrom":makeQuery(id+"F5.opRevolve","SWEPT_BODY",BODY,{"disambiguationData":[OSD([sQuery(id+"F3.wireOp",EDGE,"E6.left"),sQuery(id+"F3.wireOp",EDGE,"E6.right"),sQuery(id+"F3.wireOp",EDGE,"E14.0.1.1"),sQuery(id+"F3.wireOp",EDGE,"E14.0.2.0")])]}),"instanceName":"1"});
            var Q23;
            Q23=makeQuery(id+"F6.opPattern","COPY",BODY,{"derivedFrom":makeQuery(id+"F5.opRevolve","SWEPT_BODY",BODY,{"disambiguationData":[OSD([sQuery(id+"F3.wireOp",EDGE,"E6.left"),sQuery(id+"F3.wireOp",EDGE,"E6.right"),sQuery(id+"F3.wireOp",EDGE,"E13.bottom"),sQuery(id+"F3.wireOp",EDGE,"E14.0.1.0")])]}),"instanceName":"1"});
            var Q24;
            Q24=makeQuery(id+"F6.opPattern","COPY",BODY,{"derivedFrom":makeQuery(id+"F5.opRevolve","SWEPT_BODY",BODY,{"disambiguationData":[OSD([sQuery(id+"F3.wireOp",EDGE,"E6.left"),sQuery(id+"F3.wireOp",EDGE,"E6.right"),sQuery(id+"F3.wireOp",EDGE,"E14.0.11.1"),sQuery(id+"F3.wireOp",EDGE,"E14.0.12.0")])]}),"instanceName":"2"});
            var Q25;
            Q25=makeQuery(id+"F6.opPattern","COPY",BODY,{"derivedFrom":makeQuery(id+"F5.opRevolve","SWEPT_BODY",BODY,{"disambiguationData":[OSD([sQuery(id+"F3.wireOp",EDGE,"E6.left"),sQuery(id+"F3.wireOp",EDGE,"E6.right"),sQuery(id+"F3.wireOp",EDGE,"E14.0.10.1"),sQuery(id+"F3.wireOp",EDGE,"E14.0.11.0")])]}),"instanceName":"2"});
            var Q26;
            Q26=makeQuery(id+"F6.opPattern","COPY",BODY,{"derivedFrom":makeQuery(id+"F5.opRevolve","SWEPT_BODY",BODY,{"disambiguationData":[OSD([sQuery(id+"F3.wireOp",EDGE,"E6.left"),sQuery(id+"F3.wireOp",EDGE,"E6.right"),sQuery(id+"F3.wireOp",EDGE,"E14.0.9.1"),sQuery(id+"F3.wireOp",EDGE,"E14.0.10.0")])]}),"instanceName":"2"});
            var Q27;
            Q27=makeQuery(id+"F6.opPattern","COPY",BODY,{"derivedFrom":makeQuery(id+"F5.opRevolve","SWEPT_BODY",BODY,{"disambiguationData":[OSD([sQuery(id+"F3.wireOp",EDGE,"E6.left"),sQuery(id+"F3.wireOp",EDGE,"E6.right"),sQuery(id+"F3.wireOp",EDGE,"E14.0.8.1"),sQuery(id+"F3.wireOp",EDGE,"E14.0.9.0")])]}),"instanceName":"2"});
            var Q28;
            Q28=makeQuery(id+"F6.opPattern","COPY",BODY,{"derivedFrom":makeQuery(id+"F5.opRevolve","SWEPT_BODY",BODY,{"disambiguationData":[OSD([sQuery(id+"F3.wireOp",EDGE,"E6.left"),sQuery(id+"F3.wireOp",EDGE,"E6.right"),sQuery(id+"F3.wireOp",EDGE,"E14.0.7.1"),sQuery(id+"F3.wireOp",EDGE,"E14.0.8.0")])]}),"instanceName":"2"});
            var Q29;
            Q29=makeQuery(id+"F6.opPattern","COPY",BODY,{"derivedFrom":makeQuery(id+"F5.opRevolve","SWEPT_BODY",BODY,{"disambiguationData":[OSD([sQuery(id+"F3.wireOp",EDGE,"E6.left"),sQuery(id+"F3.wireOp",EDGE,"E6.right"),sQuery(id+"F3.wireOp",EDGE,"E14.0.6.1"),sQuery(id+"F3.wireOp",EDGE,"E14.0.7.0")])]}),"instanceName":"2"});
            var Q30;
            Q30=makeQuery(id+"F6.opPattern","COPY",BODY,{"derivedFrom":makeQuery(id+"F5.opRevolve","SWEPT_BODY",BODY,{"disambiguationData":[OSD([sQuery(id+"F3.wireOp",EDGE,"E6.left"),sQuery(id+"F3.wireOp",EDGE,"E6.right"),sQuery(id+"F3.wireOp",EDGE,"E14.0.5.1"),sQuery(id+"F3.wireOp",EDGE,"E14.0.6.0")])]}),"instanceName":"2"});
            var Q31;
            Q31=makeQuery(id+"F6.opPattern","COPY",BODY,{"derivedFrom":makeQuery(id+"F5.opRevolve","SWEPT_BODY",BODY,{"disambiguationData":[OSD([sQuery(id+"F3.wireOp",EDGE,"E6.left"),sQuery(id+"F3.wireOp",EDGE,"E6.right"),sQuery(id+"F3.wireOp",EDGE,"E14.0.4.1"),sQuery(id+"F3.wireOp",EDGE,"E14.0.5.0")])]}),"instanceName":"2"});
            var Q32;
            Q32=makeQuery(id+"F6.opPattern","COPY",BODY,{"derivedFrom":makeQuery(id+"F5.opRevolve","SWEPT_BODY",BODY,{"disambiguationData":[OSD([sQuery(id+"F3.wireOp",EDGE,"E6.left"),sQuery(id+"F3.wireOp",EDGE,"E6.right"),sQuery(id+"F3.wireOp",EDGE,"E14.0.3.1"),sQuery(id+"F3.wireOp",EDGE,"E14.0.4.0")])]}),"instanceName":"2"});
            var Q33;
            Q33=makeQuery(id+"F6.opPattern","COPY",BODY,{"derivedFrom":makeQuery(id+"F5.opRevolve","SWEPT_BODY",BODY,{"disambiguationData":[OSD([sQuery(id+"F3.wireOp",EDGE,"E6.left"),sQuery(id+"F3.wireOp",EDGE,"E6.right"),sQuery(id+"F3.wireOp",EDGE,"E14.0.2.1"),sQuery(id+"F3.wireOp",EDGE,"E14.0.3.0")])]}),"instanceName":"2"});
            var Q34;
            Q34=makeQuery(id+"F6.opPattern","COPY",BODY,{"derivedFrom":makeQuery(id+"F5.opRevolve","SWEPT_BODY",BODY,{"disambiguationData":[OSD([sQuery(id+"F3.wireOp",EDGE,"E6.left"),sQuery(id+"F3.wireOp",EDGE,"E6.right"),sQuery(id+"F3.wireOp",EDGE,"E14.0.1.1"),sQuery(id+"F3.wireOp",EDGE,"E14.0.2.0")])]}),"instanceName":"2"});
            var Q35;
            Q35=makeQuery(id+"F6.opPattern","COPY",BODY,{"derivedFrom":makeQuery(id+"F5.opRevolve","SWEPT_BODY",BODY,{"disambiguationData":[OSD([sQuery(id+"F3.wireOp",EDGE,"E6.left"),sQuery(id+"F3.wireOp",EDGE,"E6.right"),sQuery(id+"F3.wireOp",EDGE,"E13.bottom"),sQuery(id+"F3.wireOp",EDGE,"E14.0.1.0")])]}),"instanceName":"2"});
            var Q36;
            Q36=makeQuery(id+"F6.opPattern","COPY",BODY,{"derivedFrom":makeQuery(id+"F5.opRevolve","SWEPT_BODY",BODY,{"disambiguationData":[OSD([sQuery(id+"F3.wireOp",EDGE,"E6.left"),sQuery(id+"F3.wireOp",EDGE,"E6.right"),sQuery(id+"F3.wireOp",EDGE,"E14.0.11.1"),sQuery(id+"F3.wireOp",EDGE,"E14.0.12.0")])]}),"instanceName":"3"});
            var Q37;
            Q37=makeQuery(id+"F6.opPattern","COPY",BODY,{"derivedFrom":makeQuery(id+"F5.opRevolve","SWEPT_BODY",BODY,{"disambiguationData":[OSD([sQuery(id+"F3.wireOp",EDGE,"E6.left"),sQuery(id+"F3.wireOp",EDGE,"E6.right"),sQuery(id+"F3.wireOp",EDGE,"E14.0.10.1"),sQuery(id+"F3.wireOp",EDGE,"E14.0.11.0")])]}),"instanceName":"3"});
            var Q38;
            Q38=makeQuery(id+"F6.opPattern","COPY",BODY,{"derivedFrom":makeQuery(id+"F5.opRevolve","SWEPT_BODY",BODY,{"disambiguationData":[OSD([sQuery(id+"F3.wireOp",EDGE,"E6.left"),sQuery(id+"F3.wireOp",EDGE,"E6.right"),sQuery(id+"F3.wireOp",EDGE,"E14.0.9.1"),sQuery(id+"F3.wireOp",EDGE,"E14.0.10.0")])]}),"instanceName":"3"});
            var Q39;
            Q39=makeQuery(id+"F6.opPattern","COPY",BODY,{"derivedFrom":makeQuery(id+"F5.opRevolve","SWEPT_BODY",BODY,{"disambiguationData":[OSD([sQuery(id+"F3.wireOp",EDGE,"E6.left"),sQuery(id+"F3.wireOp",EDGE,"E6.right"),sQuery(id+"F3.wireOp",EDGE,"E14.0.8.1"),sQuery(id+"F3.wireOp",EDGE,"E14.0.9.0")])]}),"instanceName":"3"});
            var Q40;
            Q40=makeQuery(id+"F6.opPattern","COPY",BODY,{"derivedFrom":makeQuery(id+"F5.opRevolve","SWEPT_BODY",BODY,{"disambiguationData":[OSD([sQuery(id+"F3.wireOp",EDGE,"E6.left"),sQuery(id+"F3.wireOp",EDGE,"E6.right"),sQuery(id+"F3.wireOp",EDGE,"E14.0.7.1"),sQuery(id+"F3.wireOp",EDGE,"E14.0.8.0")])]}),"instanceName":"3"});
            var Q41;
            Q41=makeQuery(id+"F6.opPattern","COPY",BODY,{"derivedFrom":makeQuery(id+"F5.opRevolve","SWEPT_BODY",BODY,{"disambiguationData":[OSD([sQuery(id+"F3.wireOp",EDGE,"E6.left"),sQuery(id+"F3.wireOp",EDGE,"E6.right"),sQuery(id+"F3.wireOp",EDGE,"E14.0.6.1"),sQuery(id+"F3.wireOp",EDGE,"E14.0.7.0")])]}),"instanceName":"3"});
            var Q42;
            Q42=makeQuery(id+"F6.opPattern","COPY",BODY,{"derivedFrom":makeQuery(id+"F5.opRevolve","SWEPT_BODY",BODY,{"disambiguationData":[OSD([sQuery(id+"F3.wireOp",EDGE,"E6.left"),sQuery(id+"F3.wireOp",EDGE,"E6.right"),sQuery(id+"F3.wireOp",EDGE,"E14.0.5.1"),sQuery(id+"F3.wireOp",EDGE,"E14.0.6.0")])]}),"instanceName":"3"});
            var Q43;
            Q43=makeQuery(id+"F6.opPattern","COPY",BODY,{"derivedFrom":makeQuery(id+"F5.opRevolve","SWEPT_BODY",BODY,{"disambiguationData":[OSD([sQuery(id+"F3.wireOp",EDGE,"E6.left"),sQuery(id+"F3.wireOp",EDGE,"E6.right"),sQuery(id+"F3.wireOp",EDGE,"E14.0.4.1"),sQuery(id+"F3.wireOp",EDGE,"E14.0.5.0")])]}),"instanceName":"3"});
            var Q44;
            Q44=makeQuery(id+"F6.opPattern","COPY",BODY,{"derivedFrom":makeQuery(id+"F5.opRevolve","SWEPT_BODY",BODY,{"disambiguationData":[OSD([sQuery(id+"F3.wireOp",EDGE,"E6.left"),sQuery(id+"F3.wireOp",EDGE,"E6.right"),sQuery(id+"F3.wireOp",EDGE,"E14.0.3.1"),sQuery(id+"F3.wireOp",EDGE,"E14.0.4.0")])]}),"instanceName":"3"});
            var Q45;
            Q45=makeQuery(id+"F6.opPattern","COPY",BODY,{"derivedFrom":makeQuery(id+"F5.opRevolve","SWEPT_BODY",BODY,{"disambiguationData":[OSD([sQuery(id+"F3.wireOp",EDGE,"E6.left"),sQuery(id+"F3.wireOp",EDGE,"E6.right"),sQuery(id+"F3.wireOp",EDGE,"E14.0.2.1"),sQuery(id+"F3.wireOp",EDGE,"E14.0.3.0")])]}),"instanceName":"3"});
            var Q46;
            Q46=makeQuery(id+"F6.opPattern","COPY",BODY,{"derivedFrom":makeQuery(id+"F5.opRevolve","SWEPT_BODY",BODY,{"disambiguationData":[OSD([sQuery(id+"F3.wireOp",EDGE,"E6.left"),sQuery(id+"F3.wireOp",EDGE,"E6.right"),sQuery(id+"F3.wireOp",EDGE,"E14.0.1.1"),sQuery(id+"F3.wireOp",EDGE,"E14.0.2.0")])]}),"instanceName":"3"});
            var Q47;
            Q47=makeQuery(id+"F6.opPattern","COPY",BODY,{"derivedFrom":makeQuery(id+"F5.opRevolve","SWEPT_BODY",BODY,{"disambiguationData":[OSD([sQuery(id+"F3.wireOp",EDGE,"E6.left"),sQuery(id+"F3.wireOp",EDGE,"E6.right"),sQuery(id+"F3.wireOp",EDGE,"E13.bottom"),sQuery(id+"F3.wireOp",EDGE,"E14.0.1.0")])]}),"instanceName":"3"});
            var Q48;
            Q48=makeQuery(id+"F6.opPattern","COPY",BODY,{"derivedFrom":makeQuery(id+"F5.opRevolve","SWEPT_BODY",BODY,{"disambiguationData":[OSD([sQuery(id+"F3.wireOp",EDGE,"E6.left"),sQuery(id+"F3.wireOp",EDGE,"E6.right"),sQuery(id+"F3.wireOp",EDGE,"E14.0.11.1"),sQuery(id+"F3.wireOp",EDGE,"E14.0.12.0")])]}),"instanceName":"4"});
            var Q49;
            Q49=makeQuery(id+"F6.opPattern","COPY",BODY,{"derivedFrom":makeQuery(id+"F5.opRevolve","SWEPT_BODY",BODY,{"disambiguationData":[OSD([sQuery(id+"F3.wireOp",EDGE,"E6.left"),sQuery(id+"F3.wireOp",EDGE,"E6.right"),sQuery(id+"F3.wireOp",EDGE,"E14.0.10.1"),sQuery(id+"F3.wireOp",EDGE,"E14.0.11.0")])]}),"instanceName":"4"});
            var Q50;
            Q50=makeQuery(id+"F6.opPattern","COPY",BODY,{"derivedFrom":makeQuery(id+"F5.opRevolve","SWEPT_BODY",BODY,{"disambiguationData":[OSD([sQuery(id+"F3.wireOp",EDGE,"E6.left"),sQuery(id+"F3.wireOp",EDGE,"E6.right"),sQuery(id+"F3.wireOp",EDGE,"E14.0.9.1"),sQuery(id+"F3.wireOp",EDGE,"E14.0.10.0")])]}),"instanceName":"4"});
            var Q51;
            Q51=makeQuery(id+"F6.opPattern","COPY",BODY,{"derivedFrom":makeQuery(id+"F5.opRevolve","SWEPT_BODY",BODY,{"disambiguationData":[OSD([sQuery(id+"F3.wireOp",EDGE,"E6.left"),sQuery(id+"F3.wireOp",EDGE,"E6.right"),sQuery(id+"F3.wireOp",EDGE,"E14.0.8.1"),sQuery(id+"F3.wireOp",EDGE,"E14.0.9.0")])]}),"instanceName":"4"});
            var Q52;
            Q52=makeQuery(id+"F6.opPattern","COPY",BODY,{"derivedFrom":makeQuery(id+"F5.opRevolve","SWEPT_BODY",BODY,{"disambiguationData":[OSD([sQuery(id+"F3.wireOp",EDGE,"E6.left"),sQuery(id+"F3.wireOp",EDGE,"E6.right"),sQuery(id+"F3.wireOp",EDGE,"E14.0.7.1"),sQuery(id+"F3.wireOp",EDGE,"E14.0.8.0")])]}),"instanceName":"4"});
            var Q53;
            Q53=makeQuery(id+"F6.opPattern","COPY",BODY,{"derivedFrom":makeQuery(id+"F5.opRevolve","SWEPT_BODY",BODY,{"disambiguationData":[OSD([sQuery(id+"F3.wireOp",EDGE,"E6.left"),sQuery(id+"F3.wireOp",EDGE,"E6.right"),sQuery(id+"F3.wireOp",EDGE,"E14.0.6.1"),sQuery(id+"F3.wireOp",EDGE,"E14.0.7.0")])]}),"instanceName":"4"});
            var Q54;
            Q54=makeQuery(id+"F6.opPattern","COPY",BODY,{"derivedFrom":makeQuery(id+"F5.opRevolve","SWEPT_BODY",BODY,{"disambiguationData":[OSD([sQuery(id+"F3.wireOp",EDGE,"E6.left"),sQuery(id+"F3.wireOp",EDGE,"E6.right"),sQuery(id+"F3.wireOp",EDGE,"E14.0.5.1"),sQuery(id+"F3.wireOp",EDGE,"E14.0.6.0")])]}),"instanceName":"4"});
            var Q55;
            Q55=makeQuery(id+"F6.opPattern","COPY",BODY,{"derivedFrom":makeQuery(id+"F5.opRevolve","SWEPT_BODY",BODY,{"disambiguationData":[OSD([sQuery(id+"F3.wireOp",EDGE,"E6.left"),sQuery(id+"F3.wireOp",EDGE,"E6.right"),sQuery(id+"F3.wireOp",EDGE,"E14.0.4.1"),sQuery(id+"F3.wireOp",EDGE,"E14.0.5.0")])]}),"instanceName":"4"});
            var Q56;
            Q56=makeQuery(id+"F6.opPattern","COPY",BODY,{"derivedFrom":makeQuery(id+"F5.opRevolve","SWEPT_BODY",BODY,{"disambiguationData":[OSD([sQuery(id+"F3.wireOp",EDGE,"E6.left"),sQuery(id+"F3.wireOp",EDGE,"E6.right"),sQuery(id+"F3.wireOp",EDGE,"E14.0.3.1"),sQuery(id+"F3.wireOp",EDGE,"E14.0.4.0")])]}),"instanceName":"4"});
            var Q57;
            Q57=makeQuery(id+"F6.opPattern","COPY",BODY,{"derivedFrom":makeQuery(id+"F5.opRevolve","SWEPT_BODY",BODY,{"disambiguationData":[OSD([sQuery(id+"F3.wireOp",EDGE,"E6.left"),sQuery(id+"F3.wireOp",EDGE,"E6.right"),sQuery(id+"F3.wireOp",EDGE,"E14.0.2.1"),sQuery(id+"F3.wireOp",EDGE,"E14.0.3.0")])]}),"instanceName":"4"});
            var Q58;
            Q58=makeQuery(id+"F6.opPattern","COPY",BODY,{"derivedFrom":makeQuery(id+"F5.opRevolve","SWEPT_BODY",BODY,{"disambiguationData":[OSD([sQuery(id+"F3.wireOp",EDGE,"E6.left"),sQuery(id+"F3.wireOp",EDGE,"E6.right"),sQuery(id+"F3.wireOp",EDGE,"E14.0.1.1"),sQuery(id+"F3.wireOp",EDGE,"E14.0.2.0")])]}),"instanceName":"4"});
            var Q59;
            Q59=makeQuery(id+"F6.opPattern","COPY",BODY,{"derivedFrom":makeQuery(id+"F5.opRevolve","SWEPT_BODY",BODY,{"disambiguationData":[OSD([sQuery(id+"F3.wireOp",EDGE,"E6.left"),sQuery(id+"F3.wireOp",EDGE,"E6.right"),sQuery(id+"F3.wireOp",EDGE,"E13.bottom"),sQuery(id+"F3.wireOp",EDGE,"E14.0.1.0")])]}),"instanceName":"4"});
            var Q60;
            Q60=makeQuery(id+"F6.opPattern","COPY",BODY,{"derivedFrom":makeQuery(id+"F5.opRevolve","SWEPT_BODY",BODY,{"disambiguationData":[OSD([sQuery(id+"F3.wireOp",EDGE,"E6.left"),sQuery(id+"F3.wireOp",EDGE,"E6.right"),sQuery(id+"F3.wireOp",EDGE,"E14.0.11.1"),sQuery(id+"F3.wireOp",EDGE,"E14.0.12.0")])]}),"instanceName":"5"});
            var Q61;
            Q61=makeQuery(id+"F6.opPattern","COPY",BODY,{"derivedFrom":makeQuery(id+"F5.opRevolve","SWEPT_BODY",BODY,{"disambiguationData":[OSD([sQuery(id+"F3.wireOp",EDGE,"E6.left"),sQuery(id+"F3.wireOp",EDGE,"E6.right"),sQuery(id+"F3.wireOp",EDGE,"E14.0.10.1"),sQuery(id+"F3.wireOp",EDGE,"E14.0.11.0")])]}),"instanceName":"5"});
            var Q62;
            Q62=makeQuery(id+"F6.opPattern","COPY",BODY,{"derivedFrom":makeQuery(id+"F5.opRevolve","SWEPT_BODY",BODY,{"disambiguationData":[OSD([sQuery(id+"F3.wireOp",EDGE,"E6.left"),sQuery(id+"F3.wireOp",EDGE,"E6.right"),sQuery(id+"F3.wireOp",EDGE,"E14.0.9.1"),sQuery(id+"F3.wireOp",EDGE,"E14.0.10.0")])]}),"instanceName":"5"});
            var Q63;
            Q63=makeQuery(id+"F6.opPattern","COPY",BODY,{"derivedFrom":makeQuery(id+"F5.opRevolve","SWEPT_BODY",BODY,{"disambiguationData":[OSD([sQuery(id+"F3.wireOp",EDGE,"E6.left"),sQuery(id+"F3.wireOp",EDGE,"E6.right"),sQuery(id+"F3.wireOp",EDGE,"E14.0.8.1"),sQuery(id+"F3.wireOp",EDGE,"E14.0.9.0")])]}),"instanceName":"5"});
            var Q64;
            Q64=makeQuery(id+"F6.opPattern","COPY",BODY,{"derivedFrom":makeQuery(id+"F5.opRevolve","SWEPT_BODY",BODY,{"disambiguationData":[OSD([sQuery(id+"F3.wireOp",EDGE,"E6.left"),sQuery(id+"F3.wireOp",EDGE,"E6.right"),sQuery(id+"F3.wireOp",EDGE,"E14.0.7.1"),sQuery(id+"F3.wireOp",EDGE,"E14.0.8.0")])]}),"instanceName":"5"});
            var Q65;
            Q65=makeQuery(id+"F6.opPattern","COPY",BODY,{"derivedFrom":makeQuery(id+"F5.opRevolve","SWEPT_BODY",BODY,{"disambiguationData":[OSD([sQuery(id+"F3.wireOp",EDGE,"E6.left"),sQuery(id+"F3.wireOp",EDGE,"E6.right"),sQuery(id+"F3.wireOp",EDGE,"E14.0.6.1"),sQuery(id+"F3.wireOp",EDGE,"E14.0.7.0")])]}),"instanceName":"5"});
            var Q66;
            Q66=makeQuery(id+"F6.opPattern","COPY",BODY,{"derivedFrom":makeQuery(id+"F5.opRevolve","SWEPT_BODY",BODY,{"disambiguationData":[OSD([sQuery(id+"F3.wireOp",EDGE,"E6.left"),sQuery(id+"F3.wireOp",EDGE,"E6.right"),sQuery(id+"F3.wireOp",EDGE,"E14.0.5.1"),sQuery(id+"F3.wireOp",EDGE,"E14.0.6.0")])]}),"instanceName":"5"});
            var Q67;
            Q67=makeQuery(id+"F6.opPattern","COPY",BODY,{"derivedFrom":makeQuery(id+"F5.opRevolve","SWEPT_BODY",BODY,{"disambiguationData":[OSD([sQuery(id+"F3.wireOp",EDGE,"E6.left"),sQuery(id+"F3.wireOp",EDGE,"E6.right"),sQuery(id+"F3.wireOp",EDGE,"E14.0.4.1"),sQuery(id+"F3.wireOp",EDGE,"E14.0.5.0")])]}),"instanceName":"5"});
            var Q68;
            Q68=makeQuery(id+"F6.opPattern","COPY",BODY,{"derivedFrom":makeQuery(id+"F5.opRevolve","SWEPT_BODY",BODY,{"disambiguationData":[OSD([sQuery(id+"F3.wireOp",EDGE,"E6.left"),sQuery(id+"F3.wireOp",EDGE,"E6.right"),sQuery(id+"F3.wireOp",EDGE,"E14.0.3.1"),sQuery(id+"F3.wireOp",EDGE,"E14.0.4.0")])]}),"instanceName":"5"});
            var Q69;
            Q69=makeQuery(id+"F6.opPattern","COPY",BODY,{"derivedFrom":makeQuery(id+"F5.opRevolve","SWEPT_BODY",BODY,{"disambiguationData":[OSD([sQuery(id+"F3.wireOp",EDGE,"E6.left"),sQuery(id+"F3.wireOp",EDGE,"E6.right"),sQuery(id+"F3.wireOp",EDGE,"E14.0.2.1"),sQuery(id+"F3.wireOp",EDGE,"E14.0.3.0")])]}),"instanceName":"5"});
            var Q70;
            Q70=makeQuery(id+"F6.opPattern","COPY",BODY,{"derivedFrom":makeQuery(id+"F5.opRevolve","SWEPT_BODY",BODY,{"disambiguationData":[OSD([sQuery(id+"F3.wireOp",EDGE,"E6.left"),sQuery(id+"F3.wireOp",EDGE,"E6.right"),sQuery(id+"F3.wireOp",EDGE,"E14.0.1.1"),sQuery(id+"F3.wireOp",EDGE,"E14.0.2.0")])]}),"instanceName":"5"});
            var Q71;
            Q71=makeQuery(id+"F6.opPattern","COPY",BODY,{"derivedFrom":makeQuery(id+"F5.opRevolve","SWEPT_BODY",BODY,{"disambiguationData":[OSD([sQuery(id+"F3.wireOp",EDGE,"E6.left"),sQuery(id+"F3.wireOp",EDGE,"E6.right"),sQuery(id+"F3.wireOp",EDGE,"E13.bottom"),sQuery(id+"F3.wireOp",EDGE,"E14.0.1.0")])]}),"instanceName":"5"});
            var Q72;
            Q72=makeQuery(id+"F6.opPattern","COPY",BODY,{"derivedFrom":makeQuery(id+"F5.opRevolve","SWEPT_BODY",BODY,{"disambiguationData":[OSD([sQuery(id+"F3.wireOp",EDGE,"E6.left"),sQuery(id+"F3.wireOp",EDGE,"E6.right"),sQuery(id+"F3.wireOp",EDGE,"E14.0.11.1"),sQuery(id+"F3.wireOp",EDGE,"E14.0.12.0")])]}),"instanceName":"6"});
            var Q73;
            Q73=makeQuery(id+"F6.opPattern","COPY",BODY,{"derivedFrom":makeQuery(id+"F5.opRevolve","SWEPT_BODY",BODY,{"disambiguationData":[OSD([sQuery(id+"F3.wireOp",EDGE,"E6.left"),sQuery(id+"F3.wireOp",EDGE,"E6.right"),sQuery(id+"F3.wireOp",EDGE,"E14.0.10.1"),sQuery(id+"F3.wireOp",EDGE,"E14.0.11.0")])]}),"instanceName":"6"});
            var Q74;
            Q74=makeQuery(id+"F6.opPattern","COPY",BODY,{"derivedFrom":makeQuery(id+"F5.opRevolve","SWEPT_BODY",BODY,{"disambiguationData":[OSD([sQuery(id+"F3.wireOp",EDGE,"E6.left"),sQuery(id+"F3.wireOp",EDGE,"E6.right"),sQuery(id+"F3.wireOp",EDGE,"E14.0.9.1"),sQuery(id+"F3.wireOp",EDGE,"E14.0.10.0")])]}),"instanceName":"6"});
            var Q75;
            Q75=makeQuery(id+"F6.opPattern","COPY",BODY,{"derivedFrom":makeQuery(id+"F5.opRevolve","SWEPT_BODY",BODY,{"disambiguationData":[OSD([sQuery(id+"F3.wireOp",EDGE,"E6.left"),sQuery(id+"F3.wireOp",EDGE,"E6.right"),sQuery(id+"F3.wireOp",EDGE,"E14.0.8.1"),sQuery(id+"F3.wireOp",EDGE,"E14.0.9.0")])]}),"instanceName":"6"});
            var Q76;
            Q76=makeQuery(id+"F6.opPattern","COPY",BODY,{"derivedFrom":makeQuery(id+"F5.opRevolve","SWEPT_BODY",BODY,{"disambiguationData":[OSD([sQuery(id+"F3.wireOp",EDGE,"E6.left"),sQuery(id+"F3.wireOp",EDGE,"E6.right"),sQuery(id+"F3.wireOp",EDGE,"E14.0.7.1"),sQuery(id+"F3.wireOp",EDGE,"E14.0.8.0")])]}),"instanceName":"6"});
            var Q77;
            Q77=makeQuery(id+"F6.opPattern","COPY",BODY,{"derivedFrom":makeQuery(id+"F5.opRevolve","SWEPT_BODY",BODY,{"disambiguationData":[OSD([sQuery(id+"F3.wireOp",EDGE,"E6.left"),sQuery(id+"F3.wireOp",EDGE,"E6.right"),sQuery(id+"F3.wireOp",EDGE,"E14.0.6.1"),sQuery(id+"F3.wireOp",EDGE,"E14.0.7.0")])]}),"instanceName":"6"});
            var Q78;
            Q78=makeQuery(id+"F6.opPattern","COPY",BODY,{"derivedFrom":makeQuery(id+"F5.opRevolve","SWEPT_BODY",BODY,{"disambiguationData":[OSD([sQuery(id+"F3.wireOp",EDGE,"E6.left"),sQuery(id+"F3.wireOp",EDGE,"E6.right"),sQuery(id+"F3.wireOp",EDGE,"E14.0.5.1"),sQuery(id+"F3.wireOp",EDGE,"E14.0.6.0")])]}),"instanceName":"6"});
            var Q79;
            Q79=makeQuery(id+"F6.opPattern","COPY",BODY,{"derivedFrom":makeQuery(id+"F5.opRevolve","SWEPT_BODY",BODY,{"disambiguationData":[OSD([sQuery(id+"F3.wireOp",EDGE,"E6.left"),sQuery(id+"F3.wireOp",EDGE,"E6.right"),sQuery(id+"F3.wireOp",EDGE,"E14.0.4.1"),sQuery(id+"F3.wireOp",EDGE,"E14.0.5.0")])]}),"instanceName":"6"});
            var Q80;
            Q80=makeQuery(id+"F6.opPattern","COPY",BODY,{"derivedFrom":makeQuery(id+"F5.opRevolve","SWEPT_BODY",BODY,{"disambiguationData":[OSD([sQuery(id+"F3.wireOp",EDGE,"E6.left"),sQuery(id+"F3.wireOp",EDGE,"E6.right"),sQuery(id+"F3.wireOp",EDGE,"E14.0.3.1"),sQuery(id+"F3.wireOp",EDGE,"E14.0.4.0")])]}),"instanceName":"6"});
            var Q81;
            Q81=makeQuery(id+"F6.opPattern","COPY",BODY,{"derivedFrom":makeQuery(id+"F5.opRevolve","SWEPT_BODY",BODY,{"disambiguationData":[OSD([sQuery(id+"F3.wireOp",EDGE,"E6.left"),sQuery(id+"F3.wireOp",EDGE,"E6.right"),sQuery(id+"F3.wireOp",EDGE,"E14.0.2.1"),sQuery(id+"F3.wireOp",EDGE,"E14.0.3.0")])]}),"instanceName":"6"});
            var Q82;
            Q82=makeQuery(id+"F6.opPattern","COPY",BODY,{"derivedFrom":makeQuery(id+"F5.opRevolve","SWEPT_BODY",BODY,{"disambiguationData":[OSD([sQuery(id+"F3.wireOp",EDGE,"E6.left"),sQuery(id+"F3.wireOp",EDGE,"E6.right"),sQuery(id+"F3.wireOp",EDGE,"E14.0.1.1"),sQuery(id+"F3.wireOp",EDGE,"E14.0.2.0")])]}),"instanceName":"6"});
            var Q83;
            Q83=makeQuery(id+"F6.opPattern","COPY",BODY,{"derivedFrom":makeQuery(id+"F5.opRevolve","SWEPT_BODY",BODY,{"disambiguationData":[OSD([sQuery(id+"F3.wireOp",EDGE,"E6.left"),sQuery(id+"F3.wireOp",EDGE,"E6.right"),sQuery(id+"F3.wireOp",EDGE,"E13.bottom"),sQuery(id+"F3.wireOp",EDGE,"E14.0.1.0")])]}),"instanceName":"6"});
            var Q84;
            Q84=makeQuery(id+"F6.opPattern","COPY",BODY,{"derivedFrom":makeQuery(id+"F5.opRevolve","SWEPT_BODY",BODY,{"disambiguationData":[OSD([sQuery(id+"F3.wireOp",EDGE,"E6.left"),sQuery(id+"F3.wireOp",EDGE,"E6.right"),sQuery(id+"F3.wireOp",EDGE,"E14.0.11.1"),sQuery(id+"F3.wireOp",EDGE,"E14.0.12.0")])]}),"instanceName":"7"});
            var Q85;
            Q85=makeQuery(id+"F6.opPattern","COPY",BODY,{"derivedFrom":makeQuery(id+"F5.opRevolve","SWEPT_BODY",BODY,{"disambiguationData":[OSD([sQuery(id+"F3.wireOp",EDGE,"E6.left"),sQuery(id+"F3.wireOp",EDGE,"E6.right"),sQuery(id+"F3.wireOp",EDGE,"E14.0.10.1"),sQuery(id+"F3.wireOp",EDGE,"E14.0.11.0")])]}),"instanceName":"7"});
            var Q86;
            Q86=makeQuery(id+"F6.opPattern","COPY",BODY,{"derivedFrom":makeQuery(id+"F5.opRevolve","SWEPT_BODY",BODY,{"disambiguationData":[OSD([sQuery(id+"F3.wireOp",EDGE,"E6.left"),sQuery(id+"F3.wireOp",EDGE,"E6.right"),sQuery(id+"F3.wireOp",EDGE,"E14.0.9.1"),sQuery(id+"F3.wireOp",EDGE,"E14.0.10.0")])]}),"instanceName":"7"});
            var Q87;
            Q87=makeQuery(id+"F6.opPattern","COPY",BODY,{"derivedFrom":makeQuery(id+"F5.opRevolve","SWEPT_BODY",BODY,{"disambiguationData":[OSD([sQuery(id+"F3.wireOp",EDGE,"E6.left"),sQuery(id+"F3.wireOp",EDGE,"E6.right"),sQuery(id+"F3.wireOp",EDGE,"E14.0.8.1"),sQuery(id+"F3.wireOp",EDGE,"E14.0.9.0")])]}),"instanceName":"7"});
            var Q88;
            Q88=makeQuery(id+"F6.opPattern","COPY",BODY,{"derivedFrom":makeQuery(id+"F5.opRevolve","SWEPT_BODY",BODY,{"disambiguationData":[OSD([sQuery(id+"F3.wireOp",EDGE,"E6.left"),sQuery(id+"F3.wireOp",EDGE,"E6.right"),sQuery(id+"F3.wireOp",EDGE,"E14.0.7.1"),sQuery(id+"F3.wireOp",EDGE,"E14.0.8.0")])]}),"instanceName":"7"});
            var Q89;
            Q89=makeQuery(id+"F6.opPattern","COPY",BODY,{"derivedFrom":makeQuery(id+"F5.opRevolve","SWEPT_BODY",BODY,{"disambiguationData":[OSD([sQuery(id+"F3.wireOp",EDGE,"E6.left"),sQuery(id+"F3.wireOp",EDGE,"E6.right"),sQuery(id+"F3.wireOp",EDGE,"E14.0.6.1"),sQuery(id+"F3.wireOp",EDGE,"E14.0.7.0")])]}),"instanceName":"7"});
            var Q90;
            Q90=makeQuery(id+"F6.opPattern","COPY",BODY,{"derivedFrom":makeQuery(id+"F5.opRevolve","SWEPT_BODY",BODY,{"disambiguationData":[OSD([sQuery(id+"F3.wireOp",EDGE,"E6.left"),sQuery(id+"F3.wireOp",EDGE,"E6.right"),sQuery(id+"F3.wireOp",EDGE,"E14.0.5.1"),sQuery(id+"F3.wireOp",EDGE,"E14.0.6.0")])]}),"instanceName":"7"});
            var Q91;
            Q91=makeQuery(id+"F6.opPattern","COPY",BODY,{"derivedFrom":makeQuery(id+"F5.opRevolve","SWEPT_BODY",BODY,{"disambiguationData":[OSD([sQuery(id+"F3.wireOp",EDGE,"E6.left"),sQuery(id+"F3.wireOp",EDGE,"E6.right"),sQuery(id+"F3.wireOp",EDGE,"E14.0.4.1"),sQuery(id+"F3.wireOp",EDGE,"E14.0.5.0")])]}),"instanceName":"7"});
            var Q92;
            Q92=makeQuery(id+"F6.opPattern","COPY",BODY,{"derivedFrom":makeQuery(id+"F5.opRevolve","SWEPT_BODY",BODY,{"disambiguationData":[OSD([sQuery(id+"F3.wireOp",EDGE,"E6.left"),sQuery(id+"F3.wireOp",EDGE,"E6.right"),sQuery(id+"F3.wireOp",EDGE,"E14.0.3.1"),sQuery(id+"F3.wireOp",EDGE,"E14.0.4.0")])]}),"instanceName":"7"});
            var Q93;
            Q93=makeQuery(id+"F6.opPattern","COPY",BODY,{"derivedFrom":makeQuery(id+"F5.opRevolve","SWEPT_BODY",BODY,{"disambiguationData":[OSD([sQuery(id+"F3.wireOp",EDGE,"E6.left"),sQuery(id+"F3.wireOp",EDGE,"E6.right"),sQuery(id+"F3.wireOp",EDGE,"E14.0.2.1"),sQuery(id+"F3.wireOp",EDGE,"E14.0.3.0")])]}),"instanceName":"7"});
            var Q94;
            Q94=makeQuery(id+"F6.opPattern","COPY",BODY,{"derivedFrom":makeQuery(id+"F5.opRevolve","SWEPT_BODY",BODY,{"disambiguationData":[OSD([sQuery(id+"F3.wireOp",EDGE,"E6.left"),sQuery(id+"F3.wireOp",EDGE,"E6.right"),sQuery(id+"F3.wireOp",EDGE,"E14.0.1.1"),sQuery(id+"F3.wireOp",EDGE,"E14.0.2.0")])]}),"instanceName":"7"});
            var Q95;
            Q95=makeQuery(id+"F6.opPattern","COPY",BODY,{"derivedFrom":makeQuery(id+"F5.opRevolve","SWEPT_BODY",BODY,{"disambiguationData":[OSD([sQuery(id+"F3.wireOp",EDGE,"E6.left"),sQuery(id+"F3.wireOp",EDGE,"E6.right"),sQuery(id+"F3.wireOp",EDGE,"E13.bottom"),sQuery(id+"F3.wireOp",EDGE,"E14.0.1.0")])]}),"instanceName":"7"});
            var Q96;
            Q96=makeQuery(id+"F6.opPattern","COPY",BODY,{"derivedFrom":makeQuery(id+"F5.opRevolve","SWEPT_BODY",BODY,{"disambiguationData":[OSD([sQuery(id+"F3.wireOp",EDGE,"E6.left"),sQuery(id+"F3.wireOp",EDGE,"E6.right"),sQuery(id+"F3.wireOp",EDGE,"E14.0.11.1"),sQuery(id+"F3.wireOp",EDGE,"E14.0.12.0")])]}),"instanceName":"8"});
            var Q97;
            Q97=makeQuery(id+"F6.opPattern","COPY",BODY,{"derivedFrom":makeQuery(id+"F5.opRevolve","SWEPT_BODY",BODY,{"disambiguationData":[OSD([sQuery(id+"F3.wireOp",EDGE,"E6.left"),sQuery(id+"F3.wireOp",EDGE,"E6.right"),sQuery(id+"F3.wireOp",EDGE,"E14.0.10.1"),sQuery(id+"F3.wireOp",EDGE,"E14.0.11.0")])]}),"instanceName":"8"});
            var Q98;
            Q98=makeQuery(id+"F6.opPattern","COPY",BODY,{"derivedFrom":makeQuery(id+"F5.opRevolve","SWEPT_BODY",BODY,{"disambiguationData":[OSD([sQuery(id+"F3.wireOp",EDGE,"E6.left"),sQuery(id+"F3.wireOp",EDGE,"E6.right"),sQuery(id+"F3.wireOp",EDGE,"E14.0.9.1"),sQuery(id+"F3.wireOp",EDGE,"E14.0.10.0")])]}),"instanceName":"8"});
            var Q99;
            Q99=makeQuery(id+"F6.opPattern","COPY",BODY,{"derivedFrom":makeQuery(id+"F5.opRevolve","SWEPT_BODY",BODY,{"disambiguationData":[OSD([sQuery(id+"F3.wireOp",EDGE,"E6.left"),sQuery(id+"F3.wireOp",EDGE,"E6.right"),sQuery(id+"F3.wireOp",EDGE,"E14.0.8.1"),sQuery(id+"F3.wireOp",EDGE,"E14.0.9.0")])]}),"instanceName":"8"});
            var Q100;
            Q100=makeQuery(id+"F6.opPattern","COPY",BODY,{"derivedFrom":makeQuery(id+"F5.opRevolve","SWEPT_BODY",BODY,{"disambiguationData":[OSD([sQuery(id+"F3.wireOp",EDGE,"E6.left"),sQuery(id+"F3.wireOp",EDGE,"E6.right"),sQuery(id+"F3.wireOp",EDGE,"E14.0.7.1"),sQuery(id+"F3.wireOp",EDGE,"E14.0.8.0")])]}),"instanceName":"8"});
            var Q101;
            Q101=makeQuery(id+"F6.opPattern","COPY",BODY,{"derivedFrom":makeQuery(id+"F5.opRevolve","SWEPT_BODY",BODY,{"disambiguationData":[OSD([sQuery(id+"F3.wireOp",EDGE,"E6.left"),sQuery(id+"F3.wireOp",EDGE,"E6.right"),sQuery(id+"F3.wireOp",EDGE,"E14.0.6.1"),sQuery(id+"F3.wireOp",EDGE,"E14.0.7.0")])]}),"instanceName":"8"});
            var Q102;
            Q102=makeQuery(id+"F6.opPattern","COPY",BODY,{"derivedFrom":makeQuery(id+"F5.opRevolve","SWEPT_BODY",BODY,{"disambiguationData":[OSD([sQuery(id+"F3.wireOp",EDGE,"E6.left"),sQuery(id+"F3.wireOp",EDGE,"E6.right"),sQuery(id+"F3.wireOp",EDGE,"E14.0.5.1"),sQuery(id+"F3.wireOp",EDGE,"E14.0.6.0")])]}),"instanceName":"8"});
            var Q103;
            Q103=makeQuery(id+"F6.opPattern","COPY",BODY,{"derivedFrom":makeQuery(id+"F5.opRevolve","SWEPT_BODY",BODY,{"disambiguationData":[OSD([sQuery(id+"F3.wireOp",EDGE,"E6.left"),sQuery(id+"F3.wireOp",EDGE,"E6.right"),sQuery(id+"F3.wireOp",EDGE,"E14.0.4.1"),sQuery(id+"F3.wireOp",EDGE,"E14.0.5.0")])]}),"instanceName":"8"});
            var Q104;
            Q104=makeQuery(id+"F6.opPattern","COPY",BODY,{"derivedFrom":makeQuery(id+"F5.opRevolve","SWEPT_BODY",BODY,{"disambiguationData":[OSD([sQuery(id+"F3.wireOp",EDGE,"E6.left"),sQuery(id+"F3.wireOp",EDGE,"E6.right"),sQuery(id+"F3.wireOp",EDGE,"E14.0.3.1"),sQuery(id+"F3.wireOp",EDGE,"E14.0.4.0")])]}),"instanceName":"8"});
            var Q105;
            Q105=makeQuery(id+"F6.opPattern","COPY",BODY,{"derivedFrom":makeQuery(id+"F5.opRevolve","SWEPT_BODY",BODY,{"disambiguationData":[OSD([sQuery(id+"F3.wireOp",EDGE,"E6.left"),sQuery(id+"F3.wireOp",EDGE,"E6.right"),sQuery(id+"F3.wireOp",EDGE,"E14.0.2.1"),sQuery(id+"F3.wireOp",EDGE,"E14.0.3.0")])]}),"instanceName":"8"});
            var Q106;
            Q106=makeQuery(id+"F6.opPattern","COPY",BODY,{"derivedFrom":makeQuery(id+"F5.opRevolve","SWEPT_BODY",BODY,{"disambiguationData":[OSD([sQuery(id+"F3.wireOp",EDGE,"E6.left"),sQuery(id+"F3.wireOp",EDGE,"E6.right"),sQuery(id+"F3.wireOp",EDGE,"E14.0.1.1"),sQuery(id+"F3.wireOp",EDGE,"E14.0.2.0")])]}),"instanceName":"8"});
            var Q107;
            Q107=makeQuery(id+"F6.opPattern","COPY",BODY,{"derivedFrom":makeQuery(id+"F5.opRevolve","SWEPT_BODY",BODY,{"disambiguationData":[OSD([sQuery(id+"F3.wireOp",EDGE,"E6.left"),sQuery(id+"F3.wireOp",EDGE,"E6.right"),sQuery(id+"F3.wireOp",EDGE,"E13.bottom"),sQuery(id+"F3.wireOp",EDGE,"E14.0.1.0")])]}),"instanceName":"8"});
            var Q108;
            Q108=makeQuery(id+"F6.opPattern","COPY",BODY,{"derivedFrom":makeQuery(id+"F5.opRevolve","SWEPT_BODY",BODY,{"disambiguationData":[OSD([sQuery(id+"F3.wireOp",EDGE,"E6.left"),sQuery(id+"F3.wireOp",EDGE,"E6.right"),sQuery(id+"F3.wireOp",EDGE,"E14.0.11.1"),sQuery(id+"F3.wireOp",EDGE,"E14.0.12.0")])]}),"instanceName":"9"});
            var Q109;
            Q109=makeQuery(id+"F6.opPattern","COPY",BODY,{"derivedFrom":makeQuery(id+"F5.opRevolve","SWEPT_BODY",BODY,{"disambiguationData":[OSD([sQuery(id+"F3.wireOp",EDGE,"E6.left"),sQuery(id+"F3.wireOp",EDGE,"E6.right"),sQuery(id+"F3.wireOp",EDGE,"E14.0.10.1"),sQuery(id+"F3.wireOp",EDGE,"E14.0.11.0")])]}),"instanceName":"9"});
            var Q110;
            Q110=makeQuery(id+"F6.opPattern","COPY",BODY,{"derivedFrom":makeQuery(id+"F5.opRevolve","SWEPT_BODY",BODY,{"disambiguationData":[OSD([sQuery(id+"F3.wireOp",EDGE,"E6.left"),sQuery(id+"F3.wireOp",EDGE,"E6.right"),sQuery(id+"F3.wireOp",EDGE,"E14.0.9.1"),sQuery(id+"F3.wireOp",EDGE,"E14.0.10.0")])]}),"instanceName":"9"});
            var Q111;
            Q111=makeQuery(id+"F6.opPattern","COPY",BODY,{"derivedFrom":makeQuery(id+"F5.opRevolve","SWEPT_BODY",BODY,{"disambiguationData":[OSD([sQuery(id+"F3.wireOp",EDGE,"E6.left"),sQuery(id+"F3.wireOp",EDGE,"E6.right"),sQuery(id+"F3.wireOp",EDGE,"E14.0.8.1"),sQuery(id+"F3.wireOp",EDGE,"E14.0.9.0")])]}),"instanceName":"9"});
            var Q112;
            Q112=makeQuery(id+"F6.opPattern","COPY",BODY,{"derivedFrom":makeQuery(id+"F5.opRevolve","SWEPT_BODY",BODY,{"disambiguationData":[OSD([sQuery(id+"F3.wireOp",EDGE,"E6.left"),sQuery(id+"F3.wireOp",EDGE,"E6.right"),sQuery(id+"F3.wireOp",EDGE,"E14.0.7.1"),sQuery(id+"F3.wireOp",EDGE,"E14.0.8.0")])]}),"instanceName":"9"});
            var Q113;
            Q113=makeQuery(id+"F6.opPattern","COPY",BODY,{"derivedFrom":makeQuery(id+"F5.opRevolve","SWEPT_BODY",BODY,{"disambiguationData":[OSD([sQuery(id+"F3.wireOp",EDGE,"E6.left"),sQuery(id+"F3.wireOp",EDGE,"E6.right"),sQuery(id+"F3.wireOp",EDGE,"E14.0.6.1"),sQuery(id+"F3.wireOp",EDGE,"E14.0.7.0")])]}),"instanceName":"9"});
            var Q114;
            Q114=makeQuery(id+"F6.opPattern","COPY",BODY,{"derivedFrom":makeQuery(id+"F5.opRevolve","SWEPT_BODY",BODY,{"disambiguationData":[OSD([sQuery(id+"F3.wireOp",EDGE,"E6.left"),sQuery(id+"F3.wireOp",EDGE,"E6.right"),sQuery(id+"F3.wireOp",EDGE,"E14.0.5.1"),sQuery(id+"F3.wireOp",EDGE,"E14.0.6.0")])]}),"instanceName":"9"});
            var Q115;
            Q115=makeQuery(id+"F6.opPattern","COPY",BODY,{"derivedFrom":makeQuery(id+"F5.opRevolve","SWEPT_BODY",BODY,{"disambiguationData":[OSD([sQuery(id+"F3.wireOp",EDGE,"E6.left"),sQuery(id+"F3.wireOp",EDGE,"E6.right"),sQuery(id+"F3.wireOp",EDGE,"E14.0.4.1"),sQuery(id+"F3.wireOp",EDGE,"E14.0.5.0")])]}),"instanceName":"9"});
            var Q116;
            Q116=makeQuery(id+"F6.opPattern","COPY",BODY,{"derivedFrom":makeQuery(id+"F5.opRevolve","SWEPT_BODY",BODY,{"disambiguationData":[OSD([sQuery(id+"F3.wireOp",EDGE,"E6.left"),sQuery(id+"F3.wireOp",EDGE,"E6.right"),sQuery(id+"F3.wireOp",EDGE,"E14.0.3.1"),sQuery(id+"F3.wireOp",EDGE,"E14.0.4.0")])]}),"instanceName":"9"});
            var Q117;
            Q117=makeQuery(id+"F6.opPattern","COPY",BODY,{"derivedFrom":makeQuery(id+"F5.opRevolve","SWEPT_BODY",BODY,{"disambiguationData":[OSD([sQuery(id+"F3.wireOp",EDGE,"E6.left"),sQuery(id+"F3.wireOp",EDGE,"E6.right"),sQuery(id+"F3.wireOp",EDGE,"E14.0.1.1"),sQuery(id+"F3.wireOp",EDGE,"E14.0.2.0")])]}),"instanceName":"9"});
            var Q118;
            Q118=makeQuery(id+"F6.opPattern","COPY",BODY,{"derivedFrom":makeQuery(id+"F5.opRevolve","SWEPT_BODY",BODY,{"disambiguationData":[OSD([sQuery(id+"F3.wireOp",EDGE,"E6.left"),sQuery(id+"F3.wireOp",EDGE,"E6.right"),sQuery(id+"F3.wireOp",EDGE,"E13.bottom"),sQuery(id+"F3.wireOp",EDGE,"E14.0.1.0")])]}),"instanceName":"9"});
            var Q119;
            Q119=makeQuery(id+"F5.opRevolve","SWEPT_BODY",BODY,{"disambiguationData":[OSD([sQuery(id+"F3.wireOp",EDGE,"E6.left"),sQuery(id+"F3.wireOp",EDGE,"E6.right"),sQuery(id+"F3.wireOp",EDGE,"E14.0.11.1"),sQuery(id+"F3.wireOp",EDGE,"E14.0.12.0")])]});
            var Q120;
            Q120=makeQuery(id+"F4.opRevolve","SWEPT_BODY",BODY,{"disambiguationData":[OSD([sQuery(id+"F3.wireOp",EDGE,"E6.left"),sQuery(id+"F3.wireOp",EDGE,"E6.right"),sQuery(id+"F3.wireOp",EDGE,"E7.bottom"),sQuery(id+"F3.wireOp",EDGE,"E7.top"),sQuery(id+"F3.wireOp",EDGE,"E7.left"),sQuery(id+"F3.wireOp",EDGE,"E7.right"),sQuery(id+"F3.wireOp",EDGE,"E8.top"),sQuery(id+"F3.wireOp",EDGE,"E8.left"),sQuery(id+"F3.wireOp",EDGE,"E8.right"),sQuery(id+"F3.wireOp",EDGE,"E9.filletArc"),sQuery(id+"F3.wireOp",EDGE,"E10.bottom"),sQuery(id+"F3.wireOp",EDGE,"E10.top"),sQuery(id+"F3.wireOp",EDGE,"E10.left"),sQuery(id+"F3.wireOp",EDGE,"E10.right"),sQuery(id+"F3.wireOp",EDGE,"E12.top"),sQuery(id+"F3.wireOp",EDGE,"E12.left"),sQuery(id+"F3.wireOp",EDGE,"E12.right"),sQuery(id+"F3.wireOp",EDGE,"E13.left"),sQuery(id+"F3.wireOp",EDGE,"E13.right")])]});
            booleanBodies(context, id + "F7", {"operationType" : BooleanOperationType.SUBTRACTION, "tools" : qUnion([Q0, Q1, Q2, Q3, Q4, Q5, Q6, Q7, Q8, Q9, Q10, Q11, Q12, Q13, Q14, Q15, Q16, Q17, Q18, Q19, Q20, Q21, Q22, Q23, Q24, Q25, Q26, Q27, Q28, Q29, Q30, Q31, Q32, Q33, Q34, Q35, Q36, Q37, Q38, Q39, Q40, Q41, Q42, Q43, Q44, Q45, Q46, Q47, Q48, Q49, Q50, Q51, Q52, Q53, Q54, Q55, Q56, Q57, Q58, Q59, Q60, Q61, Q62, Q63, Q64, Q65, Q66, Q67, Q68, Q69, Q70, Q71, Q72, Q73, Q74, Q75, Q76, Q77, Q78, Q79, Q80, Q81, Q82, Q83, Q84, Q85, Q86, Q87, Q88, Q89, Q90, Q91, Q92, Q93, Q94, Q95, Q96, Q97, Q98, Q99, Q100, Q101, Q102, Q103, Q104, Q105, Q106, Q107, Q108, Q109, Q110, Q111, Q112, Q113, Q114, Q115, Q116, Q117, Q118, Q119]), "targets" : qUnion([Q120])});
        }
        {
            var Q0;
            {var subQ4=sQuery(id+"F3.wireOp",EDGE,"E16");Q0=makeQuery(id+"F3.imprint","IMPRINT",FACE,{"disambiguationData":[TD([[makeQuery(id+"F3.imprint","IMPRINT",EDGE,{"derivedFrom":subQ4}),-1.0]])]});}
            var Q1;
            Q1=sQuery(id+"F3.wireOp",EDGE,"E2");
            revolve(context, id + "F8", {"entities" : qUnion([Q0]), "axis" : qUnion([Q1]), "revolveType" : RevolveType.SYMMETRIC, "angle" : 20 * degree});
        }
        {
            var Q0;
            Q0=makeQuery(id+"F8.opRevolve","SWEPT_BODY",BODY,{"disambiguationData":[OSD([sQuery(id+"F3.wireOp",EDGE,"E6.right"),sQuery(id+"F3.wireOp",EDGE,"E10.bottom"),sQuery(id+"F3.wireOp",EDGE,"E11")])]});
            var Q1;
            Q1=sQuery(id+"F3.wireOp",EDGE,"E2");
            circularPattern(context, id + "F9", {"operationType" : NewBodyOperationType.ADD, "entities" : qUnion([Q0]), "axis" : qUnion([Q1]), "angle" : 360 * degree, "instanceCount" : 8, "equalSpace" : true});
        }
        {
            var Q0;
            Q0=makeQuery(id+"F0.imprint","IMPRINT",FACE,{"disambiguationData":[TD([[makeQuery(id+"F0.imprint","IMPRINT",EDGE,{"derivedFrom":sQuery(id+"F0.wireOp",EDGE,"E0")}),1.0]])]});
            extrude(context, id + "F10", {"entities" : qUnion([Q0]), "endBound" : BoundingType.SYMMETRIC, "depth" : 90 * mm});
        }
    });
